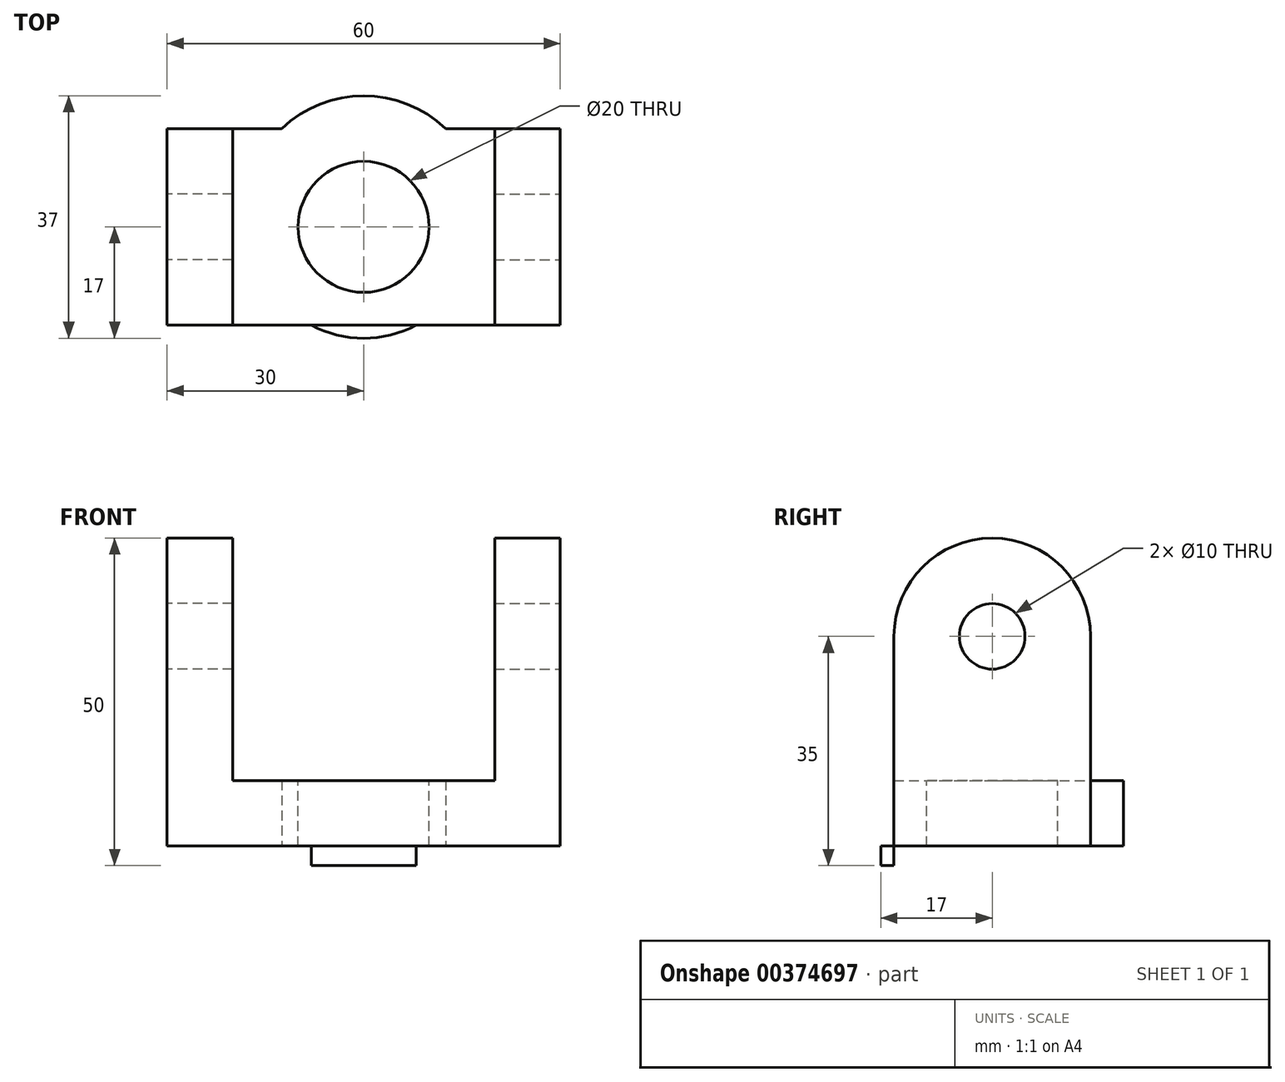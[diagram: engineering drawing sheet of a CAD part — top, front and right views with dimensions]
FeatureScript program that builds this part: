
annotation { "Feature Type Name" : "Feature", "Feature Type Description" : "" }
export const myFeature = defineFeature(function(context is Context, id is Id, definition is map)
    precondition{}
    {
        {
            var Q0;
            Q0=qCreatedBy(makeId("Top.planeOp"),FACE);
            var sketch = newSketch(context, id + "F0", { "sketchPlane" : qUnion([Q0])});
            skLineSegment(sketch, "E0", {"start": v(0, 0) * mm, "end": v(0, 30) * mm});
            skLineSegment(sketch, "E1", {"start": v(0, 30) * mm, "end": v(17.5, 30) * mm});
            skLineSegment(sketch, "E2", {"start": v(60, 30) * mm, "end": v(60, 0) * mm});
            skLineSegment(sketch, "E3", {"start": v(60, 0) * mm, "end": v(0, 0) * mm});
            skLineSegment(sketch, "E4", {"start": v(0, 30) * mm, "end": v(17.5, 30) * mm, "construction": true});
            skLineSegment(sketch, "E5", {"start": v(60, 30) * mm, "end": v(42.5, 30) * mm, "construction": true});
            skLineSegment(sketch, "E6", {"start": v(30, 30) * mm, "end": v(30, 35) * mm, "construction": true});
            skArc(sketch, "E7", {"start": v(42.5, 30) * mm, "mid": v(30, 35) * mm, "end": v(17.5, 30) * mm});
            skLineSegment(sketch, "E8.trimOffspring", {"start": v(42.5, 30) * mm, "end": v(60, 30) * mm});
            skLineSegment(sketch, "E9", {"start": v(17.5, 30) * mm, "end": v(42.5, 30) * mm, "construction": true});
            skLineSegment(sketch, "E10", {"start": v(0, 15) * mm, "end": v(60, 15) * mm, "construction": true});
            skArc(sketch, "E11.MirrorCS", {"start": v(42.5, 0) * mm, "mid": v(30, -5) * mm, "end": v(17.5, 0) * mm});
            skLineSegment(sketch, "E12.MirrorCS", {"start": v(17.5, 0) * mm, "end": v(42.5, 0) * mm, "construction": true});
            skSolve(sketch);
        }
        {
            var Q0;
            {var subQ0=sQuery(id+"F0.wireOp",EDGE,"E11.MirrorCS");Q0=makeQuery(id+"F0.imprint","IMPRINT",FACE,{"disambiguationData":[TD([[makeQuery(id+"F0.imprint","IMPRINT",EDGE,{"derivedFrom":subQ0}),-1.0]])]});}
            var Q1;
            {var subQ4=sQuery(id+"F0.wireOp",EDGE,"E0");Q1=makeQuery(id+"F0.imprint","IMPRINT",FACE,{"disambiguationData":[TD([[makeQuery(id+"F0.imprint","IMPRINT",EDGE,{"derivedFrom":subQ4}),-1.0]])]});}
            extrude(context, id + "F1", {"entities" : qUnion([Q0, Q1]), "depth" : 10 * mm});
        }
        {
            var Q0;
            Q0=makeQuery(id+"F1.opExtrude","CAP_FACE",FACE,{"disambiguationData":[OSD([sQuery(id+"F0.wireOp",EDGE,"E0"),sQuery(id+"F0.wireOp",EDGE,"E1"),sQuery(id+"F0.wireOp",EDGE,"E2"),sQuery(id+"F0.wireOp",EDGE,"E3"),sQuery(id+"F0.wireOp",EDGE,"E7"),sQuery(id+"F0.wireOp",EDGE,"E8.trimOffspring"),sQuery(id+"F0.wireOp",EDGE,"E11.MirrorCS")])],"isStart":false});
            var sketch = newSketch(context, id + "F2", { "sketchPlane" : qUnion([Q0])});
            skCircle(sketch, "E13", {"center": v(30, 15) * mm, "radius": 10 * mm});
            skSolve(sketch);
        }
        {
            var Q0;
            Q0=makeQuery(id+"F2.imprint","IMPRINT",FACE,{"disambiguationData":[TD([[makeQuery(id+"F2.imprint","IMPRINT",EDGE,{"derivedFrom":sQuery(id+"F2.wireOp",EDGE,"E13")}),1.0]])]});
            extrude(context, id + "F3", {"entities" : qUnion([Q0]), "operationType" : NewBodyOperationType.REMOVE, "endBound" : BoundingType.THROUGH_ALL, "oppositeDirection" : true, "depth" : 25 * mm});
        }
        {
            var Q0;
            Q0=makeQuery(id+"F1.opExtrude","CAP_FACE",FACE,{"disambiguationData":[OSD([sQuery(id+"F0.wireOp",EDGE,"E0"),sQuery(id+"F0.wireOp",EDGE,"E1"),sQuery(id+"F0.wireOp",EDGE,"E2"),sQuery(id+"F0.wireOp",EDGE,"E3"),sQuery(id+"F0.wireOp",EDGE,"E7"),sQuery(id+"F0.wireOp",EDGE,"E8.trimOffspring"),sQuery(id+"F0.wireOp",EDGE,"E11.MirrorCS")])],"isStart":true});
            var sketch = newSketch(context, id + "F4", { "sketchPlane" : qUnion([Q0])});
            skCircle(sketch, "E14", {"center": v(30, -15) * mm, "radius": 17 * mm});
            skCircle(sketch, "E15", {"center": v(30, -15) * mm, "radius": 10 * mm});
            skSolve(sketch);
        }
        {
            var Q0;
            Q0=makeQuery(id+"F4.imprint","IMPRINT",FACE,{"disambiguationData":[TD([[makeQuery(id+"F4.imprint","IMPRINT",EDGE,{"derivedFrom":sQuery(id+"F4.wireOp",EDGE,"E14")}),1.0]])]});
            extrude(context, id + "F5", {"entities" : qUnion([Q0]), "operationType" : NewBodyOperationType.ADD, "depth" : 3 * mm});
        }
        {
            var Q0;
            Q0=makeQuery(id+"F1.opExtrude","SWEPT_FACE",FACE,{"disambiguationData":[OSD([sQuery(id+"F0.wireOp",EDGE,"E2")])]});
            var sketch = newSketch(context, id + "F6", { "sketchPlane" : qUnion([Q0])});
            skSolve(sketch);
        }
        {
            var Q0;
            {var subQ0=sQuery(id+"F0.wireOp",EDGE,"E2");Q0=makeQuery(id+"F6.imprint","IMPRINT",FACE,{"disambiguationData":[TD([[makeQuery(id+"F6.imprint","IMPRINT",EDGE,{"derivedFrom":makeQuery(id+"F1.opExtrude","CAP_EDGE",EDGE,{"disambiguationData":[OSD([subQ0])],"isStart":true})}),-1.0]])]});}
            var sketch = newSketch(context, id + "F7", { "sketchPlane" : qUnion([Q0])});
            skLineSegment(sketch, "E16", {"start": v(0, 0) * mm, "end": v(30, 0) * mm, "construction": true});
            skLineSegment(sketch, "E17", {"start": v(15, 0) * mm, "end": v(15, 32) * mm, "construction": true});
            skCircle(sketch, "E18", {"center": v(15, 32) * mm, "radius": 5 * mm});
            skCircle(sketch, "E19", {"center": v(15, 32) * mm, "radius": 15 * mm});
            skLineSegment(sketch, "E20", {"start": v(0, 0) * mm, "end": v(0, 32) * mm});
            skLineSegment(sketch, "E21", {"start": v(0, 0) * mm, "end": v(30, 0) * mm});
            skLineSegment(sketch, "E22", {"start": v(30, 32) * mm, "end": v(30, 0) * mm});
            skSolve(sketch);
        }
        {
            var Q0;
            {var subQ5=makeQuery(id+"F6.imprint","IMPRINT",EDGE,{"derivedFrom":makeQuery(id+"F1.opExtrude","CAP_EDGE",EDGE,{"disambiguationData":[OSD([sQuery(id+"F0.wireOp",EDGE,"E2")])],"isStart":false})});Q0=makeQuery(id+"F7.imprint","IMPRINT",FACE,{"disambiguationData":[TD([[makeQuery(id+"F7.imprint","IMPRINT",EDGE,{"derivedFrom":subQ5}),-1.0]])]});}
            var Q1;
            Q1=makeQuery(id+"F7.imprint","IMPRINT",FACE,{"disambiguationData":[TD([[makeQuery(id+"F7.imprint","IMPRINT",EDGE,{"derivedFrom":sQuery(id+"F7.wireOp",EDGE,"E18")}),-1.0]])]});
            extrude(context, id + "F8", {"entities" : qUnion([Q0, Q1]), "operationType" : NewBodyOperationType.ADD, "oppositeDirection" : true, "depth" : 10 * mm});
        }
        {
            var Q0;
            Q0=makeQuery(id+"F1.opExtrude","SWEPT_FACE",FACE,{"disambiguationData":[OSD([sQuery(id+"F0.wireOp",EDGE,"E0")])]});
            var sketch = newSketch(context, id + "F9", { "sketchPlane" : qUnion([Q0])});
            skLineSegment(sketch, "E23", {"start": v(-15, 0) * mm, "end": v(-15, 32) * mm, "construction": true});
            skCircle(sketch, "E24", {"center": v(-15, 32) * mm, "radius": 5 * mm});
            skCircle(sketch, "E25", {"center": v(-15, 32) * mm, "radius": 15 * mm});
            skLineSegment(sketch, "E26", {"start": v(-30, 0) * mm, "end": v(-30, 32) * mm});
            skLineSegment(sketch, "E27", {"start": v(-30, 0) * mm, "end": v(0, 0) * mm});
            skLineSegment(sketch, "E28", {"start": v(0, 0) * mm, "end": v(0, 32) * mm});
            skSolve(sketch);
        }
        {
            var Q0;
            {var subQ5=makeQuery(id+"F1.opExtrude","CAP_EDGE",EDGE,{"disambiguationData":[OSD([sQuery(id+"F0.wireOp",EDGE,"E0")])],"isStart":false});Q0=makeQuery(id+"F9.imprint","IMPRINT",FACE,{"disambiguationData":[TD([[makeQuery(id+"F9.imprint","IMPRINT",EDGE,{"derivedFrom":subQ5}),-1.0]])]});}
            var Q1;
            Q1=makeQuery(id+"F9.imprint","IMPRINT",FACE,{"disambiguationData":[TD([[makeQuery(id+"F9.imprint","IMPRINT",EDGE,{"derivedFrom":sQuery(id+"F9.wireOp",EDGE,"E24")}),-1.0]])]});
            extrude(context, id + "F10", {"entities" : qUnion([Q0, Q1]), "operationType" : NewBodyOperationType.ADD, "oppositeDirection" : true, "depth" : 10 * mm});
        }
    });
